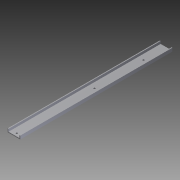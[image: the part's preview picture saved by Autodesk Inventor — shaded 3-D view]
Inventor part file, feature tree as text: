
AUTODESK INVENTOR PART (.ipt)
format: ipt  version: 2011 (Build 150239000, 239)  size: 141,824 bytes
history: native  units: in
note: dims shown in document units (in); Inventor stores cm internally (conversion verified against a paired STEP export)
features: extrude x6, sketch x6
ambient origin geometry x8: Origin, YZ Plane, XZ Plane, XY Plane, X Axis, Y Axis, Z Axis, Center Point
bodies: Solid1 (feature_tree)
feature tree (12):
  extrude  "Extrusion1"  Depth=0.374in
  extrude  "Extrusion2"  Depth=17.7165in TaperAngle=0.0deg
  extrude  "Extrusion3"  Depth=0.1693in
  extrude  "Extrusion4"  Depth=13.8583in
  extrude  "Extrusion5"  Depth=16.5in TaperAngle=0.0deg
  extrude  "Extrusion6"  Depth=2.49in
  sketch  "Sketch1"  dims[d0=1.3898in d1=0.374in]
  sketch  "Sketch2"  dims[d2=45.0deg d3=17.7165in d4=0.0in]
  sketch  "Sketch3"  dims[d5=1.0236in d6=0.1693in]
  sketch  "Sketch4"  dims[d7=15.1181in d8=13.8583in]
  sketch  "Sketch5"  dims[d9=17.7165in d10=0.0in d11=16.5in d12=0.0in]
  sketch  "Sketch6"  dims[d13=16.7812in d14=0.0in d15=2.49in d16=0.185in d17=8.0in d18=0.0925in d19=16.5in d20=16.7812in d21=0.0in d22=0.0312in d23=0.0in]
